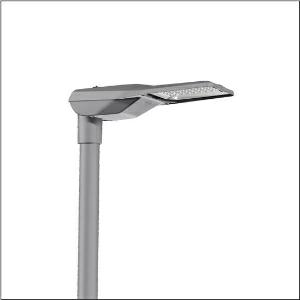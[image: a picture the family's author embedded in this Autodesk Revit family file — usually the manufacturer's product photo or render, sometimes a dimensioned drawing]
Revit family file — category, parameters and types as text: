
# Revit family: streetlight_sl_21_mini___p1_0a_5xe2a33s08gb_ad59
name_source: partatom
category: Lighting Fixtures
units: mm (PartAtom-declared; Revit-internal decimal feet)

## family parameters
Cut with Voids When Loaded = No
Host = Face
Light Source = No
Part Type = Normal
Room Calculation Point = No
Round Connector Dimension = Use Diameter
Shared = No

## types (1)
- --- (1 x LED, 5940 lm, 40.4 W, 3000K)
    Apparent Load = 40 VA
    CIE Flux Codes = 21 50 90 100 100
    Color Rendering = 70
    Color Temperature = 3000K
    Default Elevation = 1800 mm
    Description = Streetlight SL 21 mini, mast luminaire, primary light control with lens, of PMMA, primary optical cover: cover, of toughened safety glass, transparent, light distribution: P1.0a, light emission: direct distribution, primary light characteristic: asymmetric, installation type: side-entry, post-top, LED, High Power LED, rated luminous flux: 5.940lm, luminous efficacy: 147lm/W, light colour: 730, colour temperature: 3000K, control: overheat protection, constant luminous flux control, time-dependent luminous flux control, flexible luminous flux parameterisation, presetting dimming logarithmic, mains connection: 220..240V, AC, 50/60Hz, start of lifetime: 40W, end of service life: 41W, reduction: 19W, luminaire housing, of diecast aluminium, powder-coated, Siteco® metallic grey (DB 702S), corrosivity category C5 mid according to DIN EN ISO 12944, please order mast flange separately, inclination adjustable: 0°, 5°, 10°, 15°, sealing non-destructively replaceable, multi-level sealing system, length: 628mm, width: 235mm, height: 110mm, mast flange for spigot size: 42mm (side-entry): 5XC10008XM4, 60/48mm (side-entry/post-top): 5XC10108XM2, 76/60mm (side-entry/post-top): 5XC10108XM1, Smart Interface above, protection rating (complete): IP66, insulation class (complete): insulation class II (safety insulation), certification: CE, ENEC, ENEC+, VDE, impact resistance: IK09, permissible operating ambient temperature for outdoor applications: -40..+50°C, standard-compliant lighting for roads and squares, packaging unit: 1 piece

Light Distribution: P1.0a
    Height = 110 mm
    Lamp = 1 x LED
    Lamp Light Flux = 5940 lm
    Lamp Power = 40.4 W
    Lamp count = 1
    Length = 625 mm
    Luminous efficacy = 147 lm/W
    Manufacturer = Siteco
    ModVariant = No
    Model = 5XE2A33S08GB
    Number of Poles = 1
    OnlyDefault = Yes
    Power Factor = 1
    Product Name = Streetlight SL 21 mini | P1.0a
    Product group = mast luminaire | pylon top
    ProductGroupID = 6100
    Protection Class = Protection class II
    Protection Degree = IP 66
    RLX_Detail_Level = 1
    RLX_Emergency_Light_Flux = 0 lm
    RLX_Emergency_Type = 0
    RLX_Emergency_Type_DB = No
    RlxData = <blob elided: 103257 chars, md5=86a90a6f>
    Socket = socket
    Standby Power = 0 W
    System Light Flux = 5940 lm
    System Power = 40 W
    Type Comments = factory setting: luminous flux: 100 % | dim-lin: 254 | 812 mA
    Type Image = l_1003515.jpg
    URL = http://relux.com
    VarID = @adj_120199
    Voltage = 0 V
    Weight = 0.00 kg
    Width = 234 mm

## geometry (parser evidence)
native form markers: Blend x4, Sweep x9
no freeform markers — native parametric forms only
